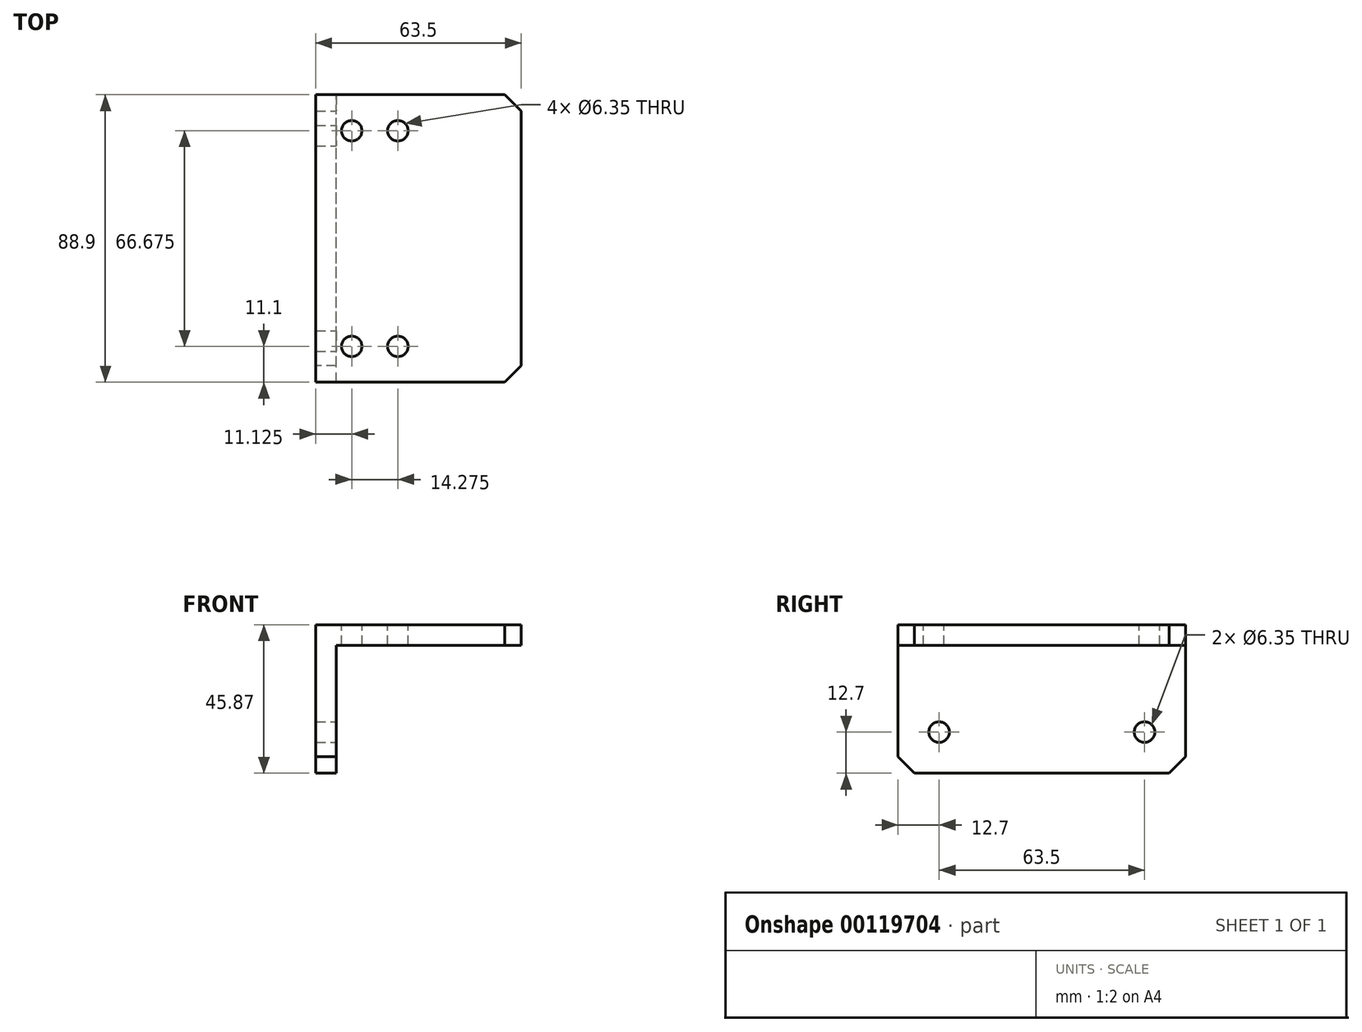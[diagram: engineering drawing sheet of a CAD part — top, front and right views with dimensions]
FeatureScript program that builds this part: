
annotation { "Feature Type Name" : "Feature", "Feature Type Description" : "" }
export const myFeature = defineFeature(function(context is Context, id is Id, definition is map)
    precondition{}
    {
        {
            var Q0;
            Q0=qCreatedBy(makeId("Front.planeOp"),FACE);
            var sketch = newSketch(context, id + "F0", { "sketchPlane" : qUnion([Q0])});
            skLineSegment(sketch, "E0", {"start": v(0, 0) * mm, "end": v(6.35, 0) * mm});
            skLineSegment(sketch, "E1", {"start": v(6.35, 0) * mm, "end": v(6.35, 39.52) * mm});
            skLineSegment(sketch, "E2", {"start": v(6.35, 39.52) * mm, "end": v(63.5, 39.52) * mm});
            skLineSegment(sketch, "E3", {"start": v(63.5, 39.52) * mm, "end": v(63.5, 45.87) * mm});
            skLineSegment(sketch, "E4", {"start": v(63.5, 45.87) * mm, "end": v(0, 45.87) * mm});
            skLineSegment(sketch, "E5", {"start": v(0, 45.87) * mm, "end": v(0, 0) * mm});
            skSolve(sketch);
        }
        {
            var Q0;
            Q0 = qSketchRegion(id + "F0", true);
            extrude(context, id + "F1", {"entities" : qUnion([Q0]), "depth" : 88.9 * mm});
        }
        {
            var Q0;
            Q0=makeQuery(id+"F1.opExtrude","SWEPT_FACE",FACE,{"disambiguationData":[OSD([sQuery(id+"F0.wireOp",EDGE,"E1")])]});
            var sketch = newSketch(context, id + "F2", { "sketchPlane" : qUnion([Q0])});
            skPoint(sketch, "E6", {"position": v(-76.2, 12.7) * mm});
            skPoint(sketch, "E7", {"position": v(-12.7, 12.7) * mm});
            skSolve(sketch);
        }
        {
            var Q0;
            Q0=sQuery(id+"F2.wireOp",VERTEX,"E6");
            var Q1;
            Q1=sQuery(id+"F2.wireOp",VERTEX,"E7");
            var Q2;
            Q2=makeQuery(id+"F1.opExtrude","SWEPT_BODY",BODY,{"disambiguationData":[OSD([sQuery(id+"F0.wireOp",EDGE,"E0"),sQuery(id+"F0.wireOp",EDGE,"E1"),sQuery(id+"F0.wireOp",EDGE,"E2"),sQuery(id+"F0.wireOp",EDGE,"E3"),sQuery(id+"F0.wireOp",EDGE,"E4"),sQuery(id+"F0.wireOp",EDGE,"E5")])]});
            hole(context, id + "F3", {"style" : HoleStyle.SIMPLE, "endStyle" : HoleEndStyle.THROUGH, "holeDiameter" : 6.35 * mm, "locations" : qUnion([Q0, Q1]), "scope" : qUnion([Q2]), "isTappedThrough" : true});
        }
        {
            var Q0;
            Q0=makeQuery(id+"F1.opExtrude","CAP_EDGE",EDGE,{"disambiguationData":[OSD([sQuery(id+"F0.wireOp",EDGE,"E0")])],"isStart":true});
            var Q1;
            Q1=makeQuery(id+"F1.opExtrude","CAP_EDGE",EDGE,{"disambiguationData":[OSD([sQuery(id+"F0.wireOp",EDGE,"E0")])],"isStart":false});
            var Q2;
            Q2=makeQuery(id+"F1.opExtrude","CAP_EDGE",EDGE,{"disambiguationData":[OSD([sQuery(id+"F0.wireOp",EDGE,"E3")])],"isStart":false});
            var Q3;
            Q3=makeQuery(id+"F1.opExtrude","CAP_EDGE",EDGE,{"disambiguationData":[OSD([sQuery(id+"F0.wireOp",EDGE,"E3")])],"isStart":true});
            chamfer(context, id + "F4", {"entities" : qUnion([Q0, Q1, Q2, Q3]), "width" : 5.08 * mm, "tangentPropagation" : true});
        }
        {
            var Q0;
            Q0=makeQuery(id+"F1.opExtrude","SWEPT_FACE",FACE,{"disambiguationData":[OSD([sQuery(id+"F0.wireOp",EDGE,"E4")])]});
            var sketch = newSketch(context, id + "F5", { "sketchPlane" : qUnion([Q0])});
            skPoint(sketch, "E8", {"position": v(11.13, -11.13) * mm});
            skPoint(sketch, "E9", {"position": v(25.4, -11.13) * mm});
            skPoint(sketch, "E10", {"position": v(25.4, -77.8) * mm});
            skPoint(sketch, "E11", {"position": v(11.13, -77.8) * mm});
            skSolve(sketch);
        }
        {
            var Q0;
            Q0=sQuery(id+"F5.wireOp",VERTEX,"E8");
            var Q1;
            Q1=sQuery(id+"F5.wireOp",VERTEX,"E9");
            var Q2;
            Q2=sQuery(id+"F5.wireOp",VERTEX,"E10");
            var Q3;
            Q3=sQuery(id+"F5.wireOp",VERTEX,"E11");
            var Q4;
            Q4=makeQuery(id+"F1.opExtrude","SWEPT_BODY",BODY,{"disambiguationData":[OSD([sQuery(id+"F0.wireOp",EDGE,"E0"),sQuery(id+"F0.wireOp",EDGE,"E1"),sQuery(id+"F0.wireOp",EDGE,"E2"),sQuery(id+"F0.wireOp",EDGE,"E3"),sQuery(id+"F0.wireOp",EDGE,"E4"),sQuery(id+"F0.wireOp",EDGE,"E5")])]});
            hole(context, id + "F6", {"style" : HoleStyle.SIMPLE, "endStyle" : HoleEndStyle.THROUGH, "holeDiameter" : 6.35 * mm, "locations" : qUnion([Q0, Q1, Q2, Q3]), "scope" : qUnion([Q4]), "isTappedThrough" : true});
        }
    });
